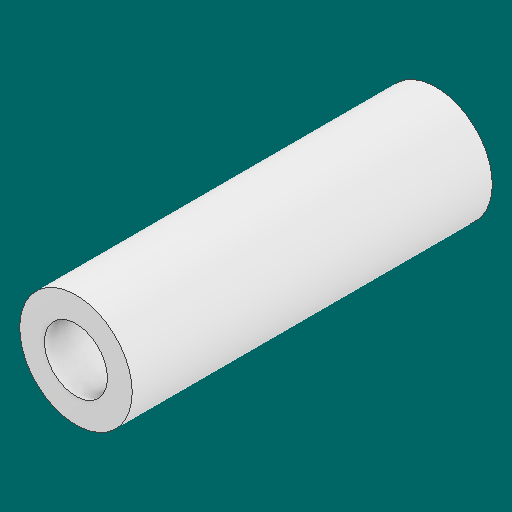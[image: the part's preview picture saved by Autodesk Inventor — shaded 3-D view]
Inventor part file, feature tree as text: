
AUTODESK INVENTOR PART (.ipt)
format: ipt  version: 2023.1 (Build 271208000, 208)  size: 103,424 bytes
history: native  units: in
note: dims shown in document units (in); Inventor stores cm internally (conversion verified against a paired STEP export)
features: extrude x1, sketch x1
ambient origin geometry x8: Origin, YZ Plane, XZ Plane, XY Plane, X Axis, Y Axis, Z Axis, Center Point
bodies: Solid1 (feature_tree)
feature tree (2):
  extrude  "Extrusion1"  Depth=1.2in
  sketch  "Sketch1"  dims[d0=0.21in d1=0.375in d2=1.2in d3=0.0in]
